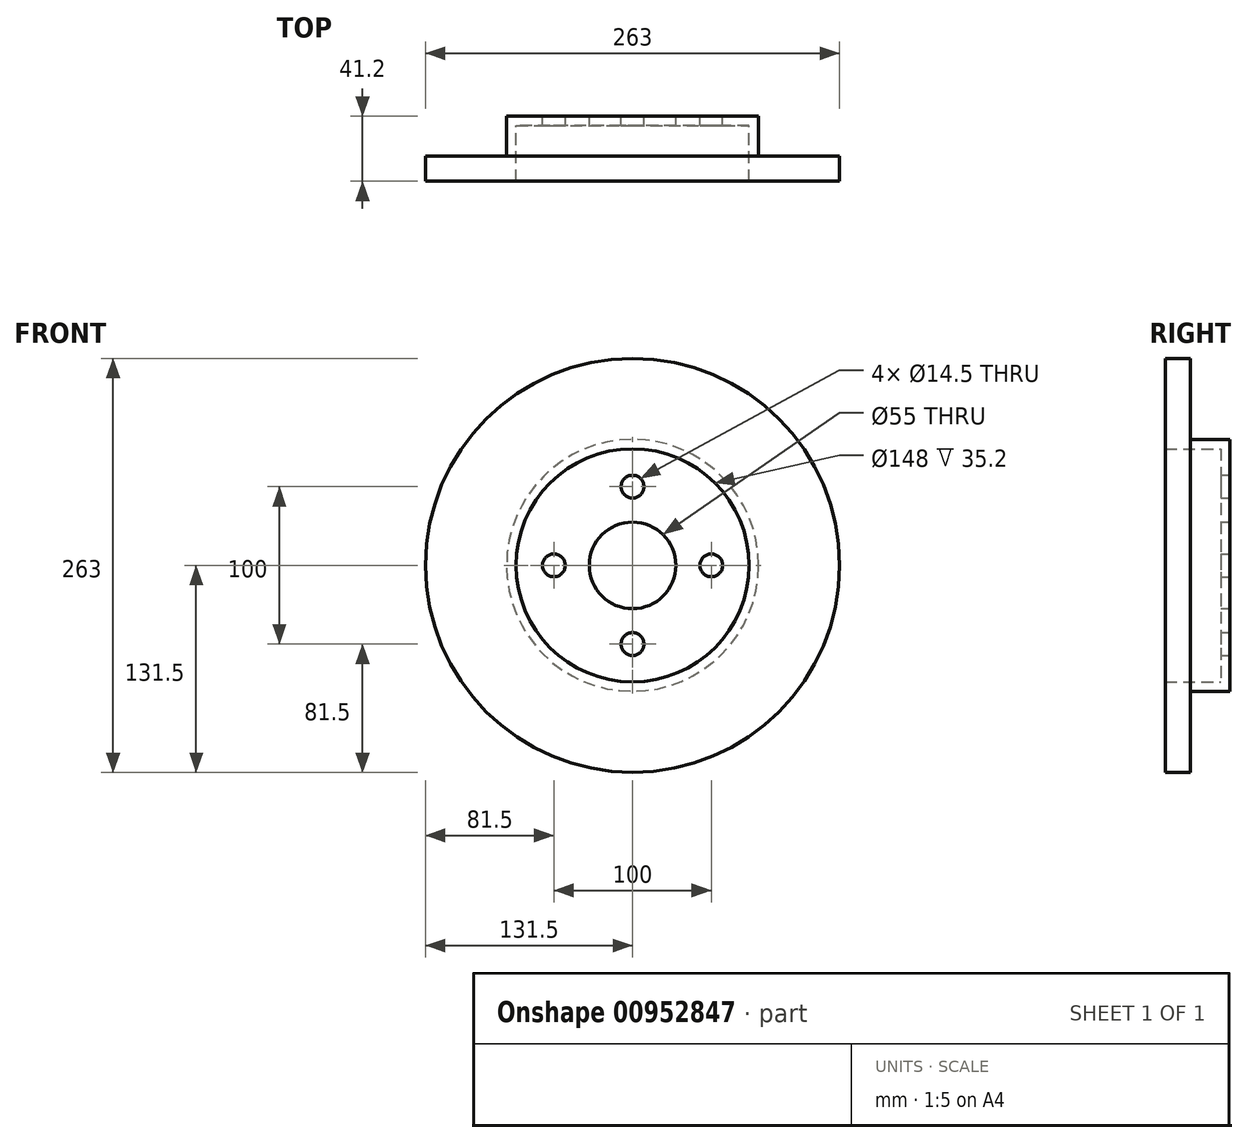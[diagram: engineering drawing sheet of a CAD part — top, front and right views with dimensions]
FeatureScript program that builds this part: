
annotation { "Feature Type Name" : "Feature", "Feature Type Description" : "" }
export const myFeature = defineFeature(function(context is Context, id is Id, definition is map)
    precondition{}
    {
        {
            var Q0;
            Q0=qCreatedBy(makeId("Right.planeOp"),FACE);
            var sketch = newSketch(context, id + "F0", { "sketchPlane" : qUnion([Q0])});
            skLineSegment(sketch, "E0", {"start": v(0, 0) * mm, "end": v(-132.22, 0) * mm, "construction": true});
            skLineSegment(sketch, "E1", {"start": v(0, 27.5) * mm, "end": v(0, 74) * mm});
            skLineSegment(sketch, "E2", {"start": v(0, 74) * mm, "end": v(-35.2, 74) * mm});
            skLineSegment(sketch, "E3", {"start": v(-35.2, 74) * mm, "end": v(-35.2, 131.5) * mm});
            skLineSegment(sketch, "E4", {"start": v(-35.2, 131.5) * mm, "end": v(-19.2, 131.5) * mm});
            skLineSegment(sketch, "E5", {"start": v(-19.2, 131.5) * mm, "end": v(-19.2, 80) * mm});
            skLineSegment(sketch, "E6", {"start": v(-19.2, 80) * mm, "end": v(6, 80) * mm});
            skLineSegment(sketch, "E7", {"start": v(6, 80) * mm, "end": v(6, 27.5) * mm});
            skLineSegment(sketch, "E8", {"start": v(6, 27.5) * mm, "end": v(0, 27.5) * mm});
            skSolve(sketch);
        }
        {
            var Q0;
            Q0 = qSketchRegion(id + "F0", true);
            var Q1;
            Q1=sQuery(id+"F0.wireOp",EDGE,"E0");
            revolve(context, id + "F1", {"surfaceOperationType" : NewSurfaceOperationType.NEW, "entities" : qUnion([Q0]), "axis" : qUnion([Q1]), "revolveType" : RevolveType.FULL});
        }
        {
            var Q0;
            Q0=makeQuery(id+"F1.opRevolve","SWEPT_FACE",FACE,{"disambiguationData":[OSD([sQuery(id+"F0.wireOp",EDGE,"E7")])]});
            var sketch = newSketch(context, id + "F2", { "sketchPlane" : qUnion([Q0])});
            skCircle(sketch, "E9.cCircle", {"center": v(0, 0) * mm, "radius": 50 * mm, "construction": true});
            skLineSegment(sketch, "E9.0", {"start": v(0, 50) * mm, "end": v(50, 0) * mm});
            skLineSegment(sketch, "E9.1", {"start": v(50, 0) * mm, "end": v(0, -50) * mm});
            skLineSegment(sketch, "E9.2", {"start": v(0, -50) * mm, "end": v(-50, 0) * mm});
            skLineSegment(sketch, "E9.3", {"start": v(-50, 0) * mm, "end": v(0, 50) * mm});
            skSolve(sketch);
        }
        {
            var Q0;
            Q0=sQuery(id+"F2.wireOp",VERTEX,"E9.0.start");
            var Q1;
            Q1=sQuery(id+"F2.wireOp",VERTEX,"E9.0.end");
            var Q2;
            Q2=sQuery(id+"F2.wireOp",VERTEX,"E9.1.end");
            var Q3;
            Q3=sQuery(id+"F2.wireOp",VERTEX,"E9.2.end");
            var Q4;
            Q4=makeQuery(id+"F1.opRevolve","SWEPT_BODY",BODY,{"disambiguationData":[OSD([sQuery(id+"F0.wireOp",EDGE,"E1"),sQuery(id+"F0.wireOp",EDGE,"E2"),sQuery(id+"F0.wireOp",EDGE,"E3"),sQuery(id+"F0.wireOp",EDGE,"E4"),sQuery(id+"F0.wireOp",EDGE,"E5"),sQuery(id+"F0.wireOp",EDGE,"E6"),sQuery(id+"F0.wireOp",EDGE,"E7"),sQuery(id+"F0.wireOp",EDGE,"E8")])]});
            hole(context, id + "F3", {"style" : HoleStyle.SIMPLE, "endStyle" : HoleEndStyle.THROUGH, "standardTappedOrClearance" : lookupTablePath({ "standard" : "ISO", "size" : "14.5", "type" : "Drilled" }), "standardBlindInLast" : lookupTablePath({ "standard" : "ISO", "size" : "14.5", "type" : "Drilled" }), "holeDiameter" : 14.5 * mm, "majorDiameter" : 5 * mm, "isTappedThrough" : true, "tappedDepth" : 12 * mm, "tapClearance" : 3, "startFromSketch" : true, "locations" : qUnion([Q0, Q1, Q2, Q3]), "scope" : qUnion([Q4])});
        }
    });
